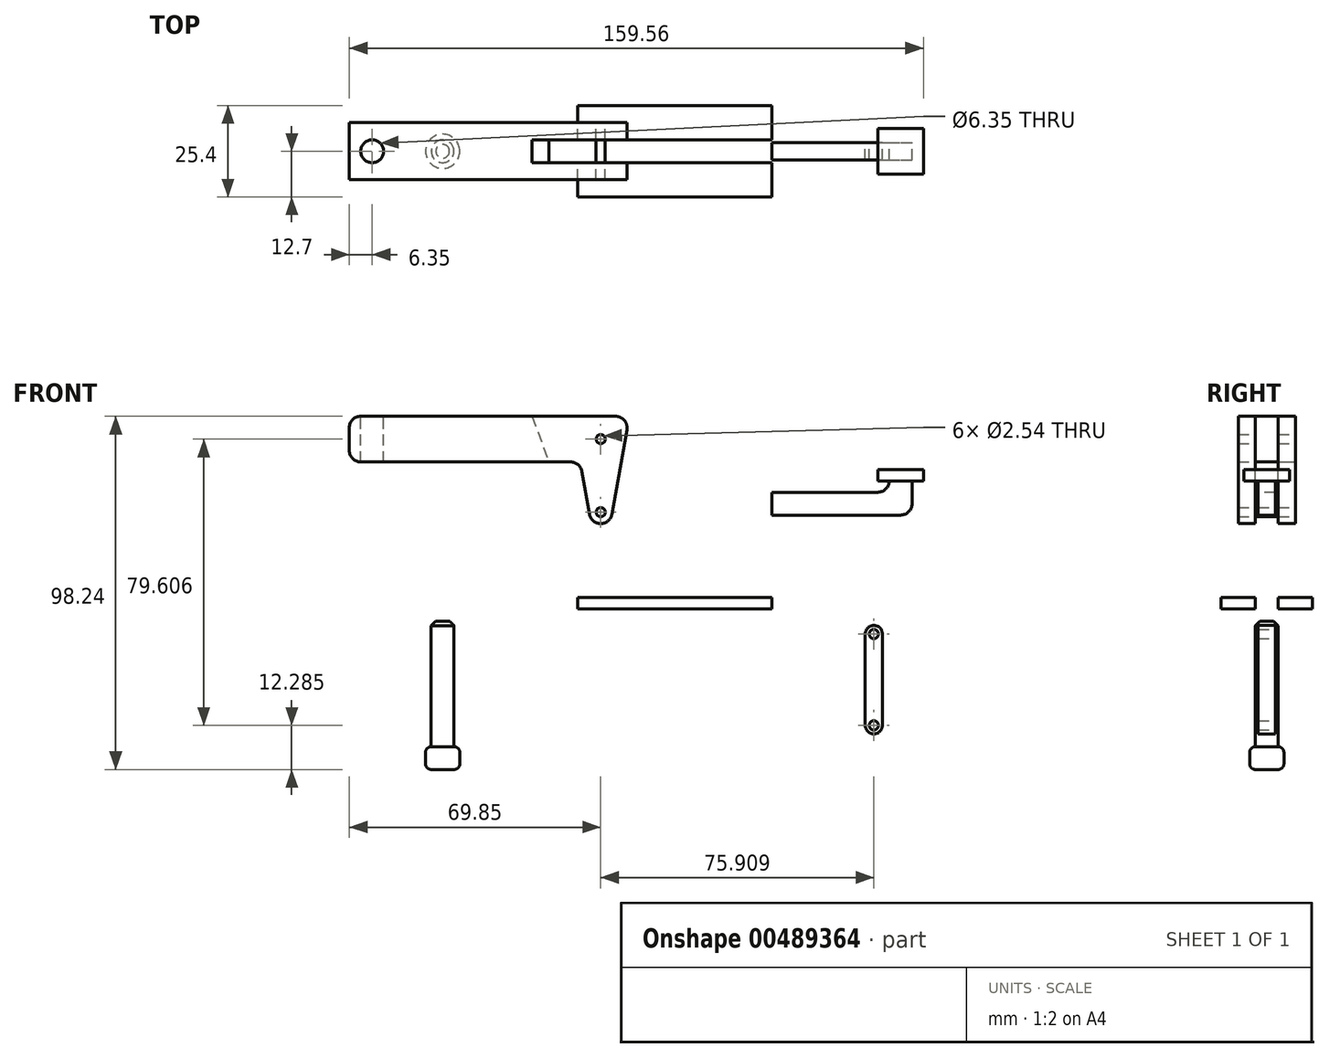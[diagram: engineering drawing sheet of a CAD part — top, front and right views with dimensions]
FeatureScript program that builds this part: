
annotation { "Feature Type Name" : "Feature", "Feature Type Description" : "" }
export const myFeature = defineFeature(function(context is Context, id is Id, definition is map)
    precondition{}
    {
        {
            var Q0;
            Q0=qCreatedBy(makeId("Front.planeOp"),FACE);
            var sketch = newSketch(context, id + "F0", { "sketchPlane" : qUnion([Q0])});
            skCircle(sketch, "E0", {"center": v(0, 0) * mm, "radius": 1.27 * mm});
            skLineSegment(sketch, "E1", {"start": v(0, 0) * mm, "end": v(59.06, 0) * mm, "construction": true});
            skLineSegment(sketch, "E2", {"start": v(0, 0) * mm, "end": v(-17.96, 17.96) * mm, "construction": true});
            skCircle(sketch, "E3", {"center": v(-17.96, 17.96) * mm, "radius": 1.27 * mm});
            skLineSegment(sketch, "E4.0", {"start": v(0, -3.18) * mm, "end": v(59.06, -3.18) * mm});
            skLineSegment(sketch, "E5.0", {"start": v(21.96, 3.18) * mm, "end": v(59.06, 3.18) * mm});
            skArc(sketch, "E6", {"start": v(-16.62, 20.84) * mm, "mid": v(-20.56, 19.78) * mm, "end": v(-20.2, 15.72) * mm});
            skLineSegment(sketch, "E7", {"start": v(-20.2, 15.72) * mm, "end": v(-2.25, -2.25) * mm});
            skLineSegment(sketch, "E8", {"start": v(-16.62, 20.84) * mm, "end": v(20.62, 3.47) * mm});
            skPoint(sketch, "E9.visualSharp", {"position": v(-1.32, -3.17) * mm});
            skPoint(sketch, "E10.visualSharp", {"position": v(21.26, 3.18) * mm});
            skArc(sketch, "E10.filletArc", {"start": v(20.62, 3.47) * mm, "mid": v(21.28, 3.25) * mm, "end": v(21.96, 3.18) * mm});
            skLineSegment(sketch, "E11", {"start": v(0, -3.17) * mm, "end": v(0, -3.18) * mm});
            skLineSegment(sketch, "E12", {"start": v(-2.25, -2.25) * mm, "end": v(-2.25, -2.25) * mm});
            skArc(sketch, "E13.filletArc", {"start": v(-2.25, -2.25) * mm, "mid": v(-1.22, -2.93) * mm, "end": v(0, -3.18) * mm});
            skArc(sketch, "E14", {"start": v(59.06, 3.18) * mm, "mid": v(61.3, 4.1) * mm, "end": v(62.23, 6.35) * mm});
            skLineSegment(sketch, "E15", {"start": v(59.06, 6.35) * mm, "end": v(71.75, 6.35) * mm});
            skLineSegment(sketch, "E16", {"start": v(68.58, 6.35) * mm, "end": v(68.58, 0) * mm});
            skLineSegment(sketch, "E17", {"start": v(65.4, -3.17) * mm, "end": v(59.06, -3.17) * mm});
            skPoint(sketch, "E18.visualSharp", {"position": v(68.58, -3.17) * mm});
            skArc(sketch, "E18.filletArc", {"start": v(65.4, -3.17) * mm, "mid": v(67.65, -2.25) * mm, "end": v(68.58, 0) * mm});
            skLineSegment(sketch, "E19", {"start": v(65.4, 6.35) * mm, "end": v(65.4, -3.17) * mm, "construction": true});
            skPoint(sketch, "E20", {"position": v(65.4, 6.35) * mm});
            skLineSegment(sketch, "E21", {"start": v(71.75, 6.35) * mm, "end": v(71.75, 9.53) * mm});
            skLineSegment(sketch, "E22", {"start": v(71.75, 9.53) * mm, "end": v(59.06, 9.53) * mm});
            skLineSegment(sketch, "E23", {"start": v(59.06, 9.53) * mm, "end": v(59.06, 6.35) * mm});
            skSolve(sketch);
        }
        {
            var Q0;
            Q0=qCreatedBy(makeId("Front.planeOp"),FACE);
            var sketch = newSketch(context, id + "F1", { "sketchPlane" : qUnion([Q0])});
            skCircle(sketch, "E24.0", {"center": v(-17.96, 17.96) * mm, "radius": 1.27 * mm});
            skCircle(sketch, "E25", {"center": v(-17.96, -2.36) * mm, "radius": 1.27 * mm});
            skCircle(sketch, "E26", {"center": v(-17.96, -2.36) * mm, "radius": 3.18 * mm});
            skLineSegment(sketch, "E27", {"start": v(-14.83, -2.91) * mm, "end": v(-10.7, 20.58) * mm});
            skLineSegment(sketch, "E28", {"start": v(-21.09, -2.91) * mm, "end": v(-23.19, 8.99) * mm});
            skLineSegment(sketch, "E29", {"start": v(-84.64, 24.31) * mm, "end": v(-13.82, 24.31) * mm});
            skLineSegment(sketch, "E30", {"start": v(-26.31, 11.61) * mm, "end": v(-84.64, 11.61) * mm});
            skPoint(sketch, "E31.visualSharp", {"position": v(-10.03, 24.31) * mm});
            skArc(sketch, "E31.filletArc", {"start": v(-10.7, 20.58) * mm, "mid": v(-11.39, 23.18) * mm, "end": v(-13.82, 24.31) * mm});
            skArc(sketch, "E32.filletArc", {"start": v(-23.19, 8.99) * mm, "mid": v(-24.27, 10.87) * mm, "end": v(-26.31, 11.61) * mm});
            skPoint(sketch, "E33.end.orphan", {"position": v(-17.96, 11.61) * mm});
            skLineSegment(sketch, "E34", {"start": v(-87.81, 21.14) * mm, "end": v(-87.81, 14.79) * mm});
            skPoint(sketch, "E35.visualSharp", {"position": v(-87.81, 24.31) * mm});
            skArc(sketch, "E35.filletArc", {"start": v(-84.64, 24.31) * mm, "mid": v(-86.88, 23.38) * mm, "end": v(-87.81, 21.14) * mm});
            skPoint(sketch, "E36.visualSharp", {"position": v(-87.81, 11.61) * mm});
            skArc(sketch, "E36.filletArc", {"start": v(-87.81, 14.79) * mm, "mid": v(-86.88, 12.54) * mm, "end": v(-84.64, 11.61) * mm});
            skLineSegment(sketch, "E37", {"start": v(-81.46, 24.31) * mm, "end": v(-81.46, 11.61) * mm, "construction": true});
            skSolve(sketch);
        }
        {
            var Q0;
            Q0=qCreatedBy(makeId("Front.planeOp"),FACE);
            var sketch = newSketch(context, id + "F2", { "sketchPlane" : qUnion([Q0])});
            skCircle(sketch, "E38.0", {"center": v(-17.96, -2.36) * mm, "radius": 1.27 * mm});
            skArc(sketch, "E39", {"start": v(-12.46, 0.82) * mm, "mid": v(-19.6, 3.77) * mm, "end": v(-24.31, -2.36) * mm});
            skLineSegment(sketch, "E40", {"start": v(-24.31, -2.36) * mm, "end": v(-24.31, -29.28) * mm});
            skLineSegment(sketch, "E41", {"start": v(-24.31, -29.28) * mm, "end": v(29.66, -29.28) * mm});
            skLineSegment(sketch, "E42", {"start": v(29.66, -29.28) * mm, "end": v(29.66, -16.58) * mm});
            skLineSegment(sketch, "E43", {"start": v(29.66, -16.58) * mm, "end": v(26.3, -4.01) * mm});
            skLineSegment(sketch, "E44", {"start": v(26.3, -4.01) * mm, "end": v(19.95, -4.01) * mm});
            skLineSegment(sketch, "E45", {"start": v(19.95, -4.01) * mm, "end": v(17.68, -14.1) * mm});
            skLineSegment(sketch, "E46", {"start": v(14.58, -16.58) * mm, "end": v(-0.58, -16.58) * mm});
            skLineSegment(sketch, "E47", {"start": v(-3.33, -15) * mm, "end": v(-12.46, 0.82) * mm});
            skPoint(sketch, "E48.visualSharp", {"position": v(17.12, -16.58) * mm});
            skArc(sketch, "E48.filletArc", {"start": v(14.58, -16.58) * mm, "mid": v(16.56, -15.89) * mm, "end": v(17.68, -14.1) * mm});
            skPoint(sketch, "E49.visualSharp", {"position": v(-2.42, -16.58) * mm});
            skArc(sketch, "E49.filletArc", {"start": v(-3.33, -15) * mm, "mid": v(-2.17, -16.16) * mm, "end": v(-0.58, -16.58) * mm});
            skLineSegment(sketch, "E50", {"start": v(-24.31, -26.1) * mm, "end": v(29.66, -26.1) * mm});
            skCircle(sketch, "E51", {"center": v(23.31, -8.7) * mm, "radius": 1.27 * mm});
            skSolve(sketch);
        }
        {
            var Q0;
            Q0=qCreatedBy(makeId("Front.planeOp"),FACE);
            var sketch = newSketch(context, id + "F3", { "sketchPlane" : qUnion([Q0])});
            skCircle(sketch, "E52", {"center": v(57.95, -36.25) * mm, "radius": 1.27 * mm});
            skArc(sketch, "E53", {"start": v(60.34, -36.25) * mm, "mid": v(57.95, -33.86) * mm, "end": v(55.56, -36.25) * mm});
            skCircle(sketch, "E54", {"center": v(57.95, -61.65) * mm, "radius": 1.27 * mm});
            skArc(sketch, "E55", {"start": v(55.56, -61.65) * mm, "mid": v(57.95, -64.03) * mm, "end": v(60.34, -61.65) * mm});
            skLineSegment(sketch, "E56", {"start": v(55.56, -36.25) * mm, "end": v(55.56, -61.65) * mm});
            skLineSegment(sketch, "E57", {"start": v(60.34, -61.65) * mm, "end": v(60.34, -36.25) * mm});
            skSolve(sketch);
        }
        {
            var Q0;
            Q0=qCreatedBy(makeId("Front.planeOp"),FACE);
            var sketch = newSketch(context, id + "F4", { "sketchPlane" : qUnion([Q0])});
            skLineSegment(sketch, "E58", {"start": v(-61.89, -32.66) * mm, "end": v(-61.89, -73.93) * mm, "construction": true});
            skLineSegment(sketch, "E59", {"start": v(-58.71, -32.66) * mm, "end": v(-58.71, -67.58) * mm});
            skLineSegment(sketch, "E60.MirrorCS", {"start": v(-65.06, -32.66) * mm, "end": v(-65.06, -67.58) * mm});
            skLineSegment(sketch, "E61", {"start": v(-61.89, -73.93) * mm, "end": v(-58.72, -73.93) * mm});
            skLineSegment(sketch, "E62", {"start": v(-57.12, -72.33) * mm, "end": v(-57.12, -69.18) * mm});
            skLineSegment(sketch, "E63", {"start": v(-58.71, -67.58) * mm, "end": v(-58.72, -67.58) * mm});
            skLineSegment(sketch, "E64.MirrorCS", {"start": v(-61.89, -73.93) * mm, "end": v(-65.05, -73.93) * mm});
            skLineSegment(sketch, "E65.MirrorCS", {"start": v(-66.65, -72.33) * mm, "end": v(-66.65, -69.18) * mm});
            skLineSegment(sketch, "E66.MirrorCS", {"start": v(-65.06, -67.58) * mm, "end": v(-65.05, -67.58) * mm});
            skLineSegment(sketch, "E67", {"start": v(-65.06, -32.66) * mm, "end": v(-58.71, -32.66) * mm});
            skPoint(sketch, "E68.visualSharp", {"position": v(-66.65, -67.58) * mm});
            skArc(sketch, "E68.filletArc", {"start": v(-65.05, -67.58) * mm, "mid": v(-66.18, -68.05) * mm, "end": v(-66.65, -69.18) * mm});
            skPoint(sketch, "E69.visualSharp", {"position": v(-66.65, -73.93) * mm});
            skArc(sketch, "E69.filletArc", {"start": v(-66.65, -72.33) * mm, "mid": v(-66.18, -73.46) * mm, "end": v(-65.05, -73.93) * mm});
            skPoint(sketch, "E70.visualSharp", {"position": v(-57.12, -73.93) * mm});
            skArc(sketch, "E70.filletArc", {"start": v(-58.72, -73.93) * mm, "mid": v(-57.6, -73.46) * mm, "end": v(-57.12, -72.33) * mm});
            skPoint(sketch, "E71.visualSharp", {"position": v(-57.12, -67.58) * mm});
            skArc(sketch, "E71.filletArc", {"start": v(-57.12, -69.18) * mm, "mid": v(-57.6, -68.05) * mm, "end": v(-58.72, -67.58) * mm});
            skLineSegment(sketch, "E72", {"start": v(-61.89, -32.66) * mm, "end": v(-61.89, -73.93) * mm});
            skSolve(sketch);
        }
        {
            var Q0;
            {var subQ2=sQuery(id+"F4.wireOp",EDGE,"E59");Q0=makeQuery(id+"F4.imprint","IMPRINT",FACE,{"disambiguationData":[TD([[makeQuery(id+"F4.imprint","IMPRINT",EDGE,{"derivedFrom":subQ2}),-1.0]])]});}
            var Q1;
            Q1=sQuery(id+"F4.wireOp",EDGE,"E72");
            revolve(context, id + "F5", {"entities" : qUnion([Q0]), "axis" : qUnion([Q1]), "revolveType" : RevolveType.FULL});
        }
        {
            var Q0;
            Q0=makeQuery(id+"F5.opRevolve","SWEPT_EDGE",EDGE,{"disambiguationData":[OSD([sQuery(id+"F4.wireOp",EDGE,"E59"),sQuery(id+"F4.wireOp",EDGE,"E67")])]});
            chamfer(context, id + "F6", {"entities" : qUnion([Q0]), "chamferType" : ChamferType.OFFSET_ANGLE, "width" : 1.27 * mm, "oppositeDirection" : false, "angle" : 45 * degree, "tangentPropagation" : true});
        }
        {
            var Q0;
            Q0=makeQuery(id+"F3.imprint","IMPRINT",FACE,{"disambiguationData":[TD([[makeQuery(id+"F3.imprint","IMPRINT",EDGE,{"derivedFrom":sQuery(id+"F3.wireOp",EDGE,"E52")}),-1.0]])]});
            extrude(context, id + "F7", {"entities" : qUnion([Q0]), "endBound" : BoundingType.SYMMETRIC, "depth" : 4.78 * mm, "offsetDistance" : 25.4 * mm});
        }
        {
            var Q0;
            {var subQ0=sQuery(id+"F2.wireOp",EDGE,"E41");Q0=makeQuery(id+"F2.imprint","IMPRINT",FACE,{"disambiguationData":[TD([[makeQuery(id+"F2.imprint","IMPRINT",EDGE,{"derivedFrom":subQ0}),1.0]])]});}
            extrude(context, id + "F8", {"entities" : qUnion([Q0]), "endBound" : BoundingType.SYMMETRIC, "depth" : 25.4 * mm, "offsetDistance" : 25.4 * mm});
        }
        {
            var Q0;
            Q0=makeQuery(id+"F2.imprint","IMPRINT",FACE,{"disambiguationData":[TD([[makeQuery(id+"F2.imprint","IMPRINT",EDGE,{"derivedFrom":sQuery(id+"F2.wireOp",EDGE,"E38.0")}),-1.0]])]});
            extrude(context, id + "F9", {"entities" : qUnion([Q0]), "operationType" : NewBodyOperationType.ADD, "endBound" : BoundingType.SYMMETRIC, "depth" : 4.78 * mm, "offsetDistance" : 25.4 * mm});
        }
        {
            var Q0;
            Q0=makeQuery(id+"F0.imprint","IMPRINT",FACE,{"disambiguationData":[TD([[makeQuery(id+"F0.imprint","IMPRINT",EDGE,{"derivedFrom":sQuery(id+"F0.wireOp",EDGE,"E0")}),-1.0]])]});
            extrude(context, id + "F10", {"entities" : qUnion([Q0]), "endBound" : BoundingType.SYMMETRIC, "depth" : 4.78 * mm, "offsetDistance" : 25.4 * mm});
        }
        {
            var Q0;
            {var subQ0=sQuery(id+"F0.wireOp",EDGE,"E21");Q0=makeQuery(id+"F0.imprint","IMPRINT",FACE,{"disambiguationData":[TD([[makeQuery(id+"F0.imprint","IMPRINT",EDGE,{"derivedFrom":subQ0}),1.0]])]});}
            extrude(context, id + "F11", {"entities" : qUnion([Q0]), "operationType" : NewBodyOperationType.ADD, "endBound" : BoundingType.SYMMETRIC, "depth" : 12.7 * mm, "offsetDistance" : 25.4 * mm});
        }
        {
            var Q0;
            Q0=makeQuery(id+"F1.imprint","IMPRINT",FACE,{"disambiguationData":[TD([[makeQuery(id+"F1.imprint","IMPRINT",EDGE,{"derivedFrom":sQuery(id+"F1.wireOp",EDGE,"E24.0")}),-1.0]])]});
            var Q1;
            Q1=makeQuery(id+"F1.imprint","IMPRINT",FACE,{"disambiguationData":[TD([[makeQuery(id+"F1.imprint","IMPRINT",EDGE,{"derivedFrom":sQuery(id+"F1.wireOp",EDGE,"E25")}),-1.0]])]});
            extrude(context, id + "F12", {"entities" : qUnion([Q0, Q1]), "endBound" : BoundingType.SYMMETRIC, "depth" : 15.88 * mm, "offsetDistance" : 25.4 * mm});
        }
        {
            var Q0;
            Q0=makeQuery(id+"F8.opExtrude","SWEPT_FACE",FACE,{"disambiguationData":[OSD([sQuery(id+"F2.wireOp",EDGE,"E41")])]});
            var sketch = newSketch(context, id + "F13", { "sketchPlane" : qUnion([Q0])});
            skLineSegment(sketch, "E73", {"start": v(29.66, 2.39) * mm, "end": v(29.66, -2.39) * mm});
            skPoint(sketch, "E74", {"position": v(2.68, 12.7) * mm});
            skLineSegment(sketch, "E75.bottom", {"start": v(-24.31, 3.18) * mm, "end": v(29.66, 3.18) * mm});
            skLineSegment(sketch, "E75.top", {"start": v(-24.31, -3.18) * mm, "end": v(29.66, -3.18) * mm});
            skLineSegment(sketch, "E75.left", {"start": v(-24.31, 3.18) * mm, "end": v(-24.31, -3.18) * mm});
            skLineSegment(sketch, "E75.right", {"start": v(29.66, 3.18) * mm, "end": v(29.66, -3.18) * mm});
            skPoint(sketch, "E75.middle", {"position": v(2.68, 0) * mm});
            skLineSegment(sketch, "E76.bottom", {"start": v(-24.31, -3.18) * mm, "end": v(-37.01, -3.18) * mm});
            skLineSegment(sketch, "E76.top", {"start": v(-24.31, 3.18) * mm, "end": v(-37.01, 3.18) * mm});
            skLineSegment(sketch, "E76.left", {"start": v(-24.31, -3.18) * mm, "end": v(-24.31, 3.18) * mm});
            skLineSegment(sketch, "E76.right", {"start": v(-37.01, -3.18) * mm, "end": v(-37.01, 3.18) * mm});
            skSolve(sketch);
        }
        {
            var Q0;
            Q0=makeQuery(id+"F13.imprint","IMPRINT",FACE,{"disambiguationData":[TD([[makeQuery(id+"F13.imprint","IMPRINT",EDGE,{"derivedFrom":sQuery(id+"F13.wireOp",EDGE,"E76.bottom")}),-1.0]])]});
            var Q1;
            {var subQ0=sQuery(id+"F13.wireOp",EDGE,"E75.bottom");Q1=makeQuery(id+"F13.imprint","IMPRINT",FACE,{"disambiguationData":[TD([[makeQuery(id+"F13.imprint","IMPRINT",EDGE,{"derivedFrom":subQ0}),-1.0]])]});}
            extrude(context, id + "F14", {"entities" : qUnion([Q0, Q1]), "operationType" : NewBodyOperationType.REMOVE, "endBound" : BoundingType.THROUGH_ALL, "oppositeDirection" : true, "depth" : 25.4 * mm, "offsetDistance" : 25.4 * mm});
        }
        {
            var Q0;
            Q0=makeQuery(id+"F14.boolean.opBoolean","COPY",FACE,{"derivedFrom":makeQuery(id+"F14.opExtrude","SWEPT_FACE",FACE,{"disambiguationData":[OSD([sQuery(id+"F13.wireOp",EDGE,"E75.top"),sQuery(id+"F13.wireOp",EDGE,"E76.bottom")])]})});
            var sketch = newSketch(context, id + "F15", { "sketchPlane" : qUnion([Q0])});
            skLineSegment(sketch, "E77", {"start": v(-37.01, 24.31) * mm, "end": v(-32.39, 11.61) * mm});
            skLineSegment(sketch, "E78", {"start": v(-32.39, 11.61) * mm, "end": v(-37.01, 11.61) * mm});
            skLineSegment(sketch, "E79", {"start": v(-37.01, 11.61) * mm, "end": v(-37.01, 24.31) * mm});
            skSolve(sketch);
        }
        {
            var Q0;
            Q0=makeQuery(id+"F15.imprint","IMPRINT",FACE,{"disambiguationData":[TD([[makeQuery(id+"F15.imprint","IMPRINT",EDGE,{"derivedFrom":sQuery(id+"F15.wireOp",EDGE,"E77")}),-1.0]])]});
            extrude(context, id + "F16", {"entities" : qUnion([Q0]), "operationType" : NewBodyOperationType.ADD, "endBound" : BoundingType.UP_TO_NEXT, "depth" : 25.4 * mm, "offsetDistance" : 25.4 * mm});
        }
        {
            var Q0;
            Q0=makeQuery(id+"F12.opExtrude","SWEPT_FACE",FACE,{"disambiguationData":[OSD([sQuery(id+"F1.wireOp",EDGE,"E29")])]});
            var sketch = newSketch(context, id + "F17", { "sketchPlane" : qUnion([Q0])});
            skPoint(sketch, "E80.0", {"position": v(-81.46, 0) * mm});
            skCircle(sketch, "E81", {"center": v(-81.46, 0) * mm, "radius": 3.18 * mm});
            skSolve(sketch);
        }
        {
            var Q0;
            Q0=sQuery(id+"F17.wireOp",VERTEX,"E80.0");
            var Q1;
            Q1=makeQuery(id+"F12.opExtrude","SWEPT_BODY",BODY,{"disambiguationData":[OSD([sQuery(id+"F1.wireOp",EDGE,"E24.0"),sQuery(id+"F1.wireOp",EDGE,"E25"),sQuery(id+"F1.wireOp",EDGE,"E26"),sQuery(id+"F1.wireOp",EDGE,"E27"),sQuery(id+"F1.wireOp",EDGE,"E28"),sQuery(id+"F1.wireOp",EDGE,"E29"),sQuery(id+"F1.wireOp",EDGE,"E30"),sQuery(id+"F1.wireOp",EDGE,"E31.filletArc"),sQuery(id+"F1.wireOp",EDGE,"E32.filletArc"),sQuery(id+"F1.wireOp",EDGE,"E34"),sQuery(id+"F1.wireOp",EDGE,"E35.filletArc"),sQuery(id+"F1.wireOp",EDGE,"E36.filletArc")])]});
            hole(context, id + "F18", {"style" : HoleStyle.SIMPLE, "endStyle" : HoleEndStyle.THROUGH, "holeDiameter" : 6.35 * mm, "majorDiameter" : 6.35 * mm, "isTappedThrough" : true, "tappedDepth" : 12.7 * mm, "tapClearance" : 3, "locations" : qUnion([Q0]), "scope" : qUnion([Q1])});
        }
        {
            var Q0;
            Q0=makeQuery(id+"F1.imprint","IMPRINT",FACE,{"disambiguationData":[TD([[makeQuery(id+"F1.imprint","IMPRINT",EDGE,{"derivedFrom":sQuery(id+"F1.wireOp",EDGE,"E25")}),1.0]])]});
            var Q1;
            Q1=sQuery(id+"F1.wireOp",EDGE,"E25");
            extrude(context, id + "F19", {"entities" : qUnion([Q0]), "surfaceEntities" : qUnion([Q1]), "endBound" : BoundingType.SYMMETRIC, "depth" : 15.88 * mm, "offsetDistance" : 25.4 * mm});
        }
    });
